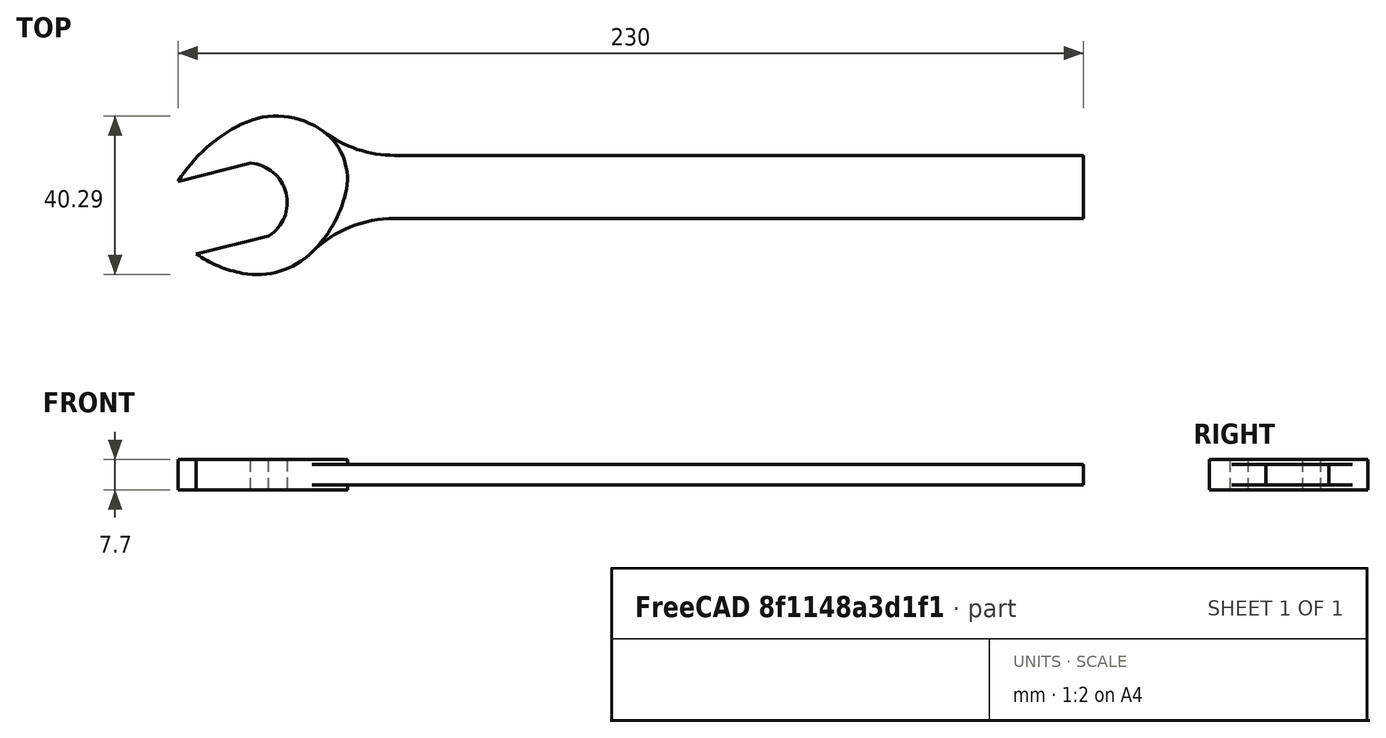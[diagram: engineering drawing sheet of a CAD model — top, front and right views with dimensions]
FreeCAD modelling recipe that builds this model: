
FCSTD DOCUMENT  (FreeCAD 0.21R33694 (Git))
Label: Spanner_Example
License: All rights reserved
LicenseURL: http://en.wikipedia.org/wiki/All_rights_reserved
objects: Sketcher::SketchObject×2, PartDesign::Pad×2, Fem::ConstraintFixed×2, PartDesign::Body×1, Fem::FemSolverObjectPython×1, Fem::FemMeshObjectPython×1, App::MaterialObjectPython×1, Fem::ConstraintPressure×1, Fem::FemAnalysis×1
note: 7 computed .brp shape members not serialized (recipe doc carries the construction recipe); baked Part::Feature solids carry a one-line shape summary decoded from their .brp

FEATURE [Sketcher::SketchObject] Sketch
  FullyConstrained = false
  MapMode = 5
  Support = -> [XY_Plane]
  sketch-geometry (10):
    g0: LineSegment StartX=-55 StartY=18.4356 StartZ=0 EndX=-36.5644 EndY=23.0321 EndZ=0
    g1: LineSegment StartX=-50.4035 StartY=-3.6e-15 StartZ=0 EndX=-31.9679 EndY=4.59652 EndZ=0
    g2: LineSegment StartX=-31.9679 StartY=4.59652 StartZ=0 EndX=-36.5644 EndY=23.0321 EndZ=0
    g3: ArcOfCircle CenterX=-37.2959 CenterY=13.0589 CenterZ=0 NormalX=0 NormalY=0 NormalZ=1 AngleXU=0 Radius=10 StartAngle=5.2743 EndAngle=7.78077
    g4: ArcOfCircle CenterX=-21.1751 CenterY=-2.91558 CenterZ=0 NormalX=0 NormalY=0 NormalZ=1 AngleXU=0 Radius=40 StartAngle=2.02778 EndAngle=2.57853
    g5: ArcOfCircle CenterX=-30 CenterY=15.0321 CenterZ=0 NormalX=0 NormalY=0 NormalZ=1 AngleXU=0 Radius=20 StartAngle=0.927295 EndAngle=2.02778
    g6: ArcOfCircle CenterX=-33.1975 CenterY=24.5755 CenterZ=0 NormalX=0 NormalY=0 NormalZ=1 AngleXU=0 Radius=30 StartAngle=4.10158 EndAngle=4.53115
    g7: ArcOfCircle CenterX=-35 CenterY=14.7393 CenterZ=0 NormalX=0 NormalY=0 NormalZ=1 AngleXU=0 Radius=20 StartAngle=4.53115 EndAngle=5.48779
    g8: ArcOfCircle CenterX=-27 CenterY=19.0321 CenterZ=0 NormalX=0 NormalY=0 NormalZ=1 AngleXU=0 Radius=15 StartAngle=6.03904 EndAngle=7.21048
    g9: ArcOfCircle CenterX=-43.1518 CenterY=23.0558 CenterZ=0 NormalX=0 NormalY=0 NormalZ=1 AngleXU=0 Radius=31.6454 StartAngle=5.48779 EndAngle=6.03904
  constraints (26):
    c: Parallel(g0,g1)
    c: Distance(g0) = 19
    c: Distance(g1) = 19
    c: Distance(g1,g0) = 19
    c: Coincident(g2,g1)
    c: Coincident(g2,g0)
    c: Perpendicular(g0,g2)
    c: Angle(g-1,g0) = 0.244346
    c: PointOnObject(g1,g-1)
    c: Coincident(g3,g0)
    c: Coincident(g3,g1)
    c: Radius(g3) = 10
    c: Coincident(g4,g0)
    c: Radius(g4) = 40
    c: Radius(g5) = 20
    c: Coincident(g6,g1)
    c: Radius(g6) = 30
    c: Radius(g7) = 20
    c: Tangent(g5,g4) = -1.5708
    c: Tangent(g7,g6) = -1.5708
    c: Distance(g7,g-2) = 21
    c: Distance(g5,g-2) = 18
    c: Tangent(g8,g5) = -1.5708
    c: Radius(g8) = 15
    c: Tangent(g9,g7) = -1.5708
    c: Tangent(g9,g8) = -1.5708
FEATURE [Sketcher::SketchObject] Sketch001
  FullyConstrained = false
  MapMode = 5
  Support = -> [XY_Plane]
  sketch-geometry (9):
    g0: ArcOfCircle CenterX=1e-16 CenterY=55.0321 CenterZ=0 NormalX=0 NormalY=0 NormalZ=1 AngleXU=0 Radius=30 StartAngle=4.06889 EndAngle=4.71239
    g1: LineSegment StartX=-5.4e-15 StartY=25.0321 StartZ=0 EndX=140 EndY=25.0321 EndZ=0
    g2: ArcOfCircle CenterX=-3.7e-15 CenterY=-20.9679 CenterZ=0 NormalX=0 NormalY=0 NormalZ=1 AngleXU=0 Radius=30 StartAngle=1.5708 EndAngle=2.34619
    g3: LineSegment StartX=-1.9e-15 StartY=9.03213 StartZ=0 EndX=140 EndY=9.03213 EndZ=0
    g4: LineSegment StartX=140 StartY=25.0321 StartZ=0 EndX=175 EndY=25.0321 EndZ=0
    g5: LineSegment StartX=140 StartY=9.03213 StartZ=0 EndX=175 EndY=9.03213 EndZ=0
    g6: LineSegment StartX=175 StartY=25.0321 StartZ=0 EndX=175 EndY=9.03213 EndZ=0
    g7: ArcOfCircle CenterX=-27 CenterY=19.0321 CenterZ=0 NormalX=0 NormalY=0 NormalZ=1 AngleXU=0 Radius=15 StartAngle=6.03904 EndAngle=7.21048
    g8: ArcOfCircle CenterX=-43.1518 CenterY=23.0558 CenterZ=0 NormalX=0 NormalY=0 NormalZ=1 AngleXU=0 Radius=31.6454 StartAngle=5.48779 EndAngle=6.03904
  constraints (20):
    c: Radius(g0) = 30
    c: Horizontal(g1)
    c: Radius(g2) = 30
    c: Horizontal(g3)
    c: Distance(g2,g1) = 16
    c: Tangent(g1,g0) = -1.5708
    c: Tangent(g3,g2) = 1.5708
    c: PointOnObject(g2,g-2)
    c: Distance(g1) = 140
    c: Distance(g3) = 140
    c: Coincident(g4,g1)
    c: Horizontal(g4)
    c: Coincident(g5,g3)
    c: Horizontal(g5)
    c: Coincident(g6,g4)
    c: Coincident(g6,g5)
    c: Vertical(g6)
    c: Distance(g4) = 35
    c: Radius(g7) = 15
    c: Tangent(g8,g7) = -1.5708
FEATURE [PartDesign::Pad] Pad
  Direction = (0,0,1)
  Length = 5.3
  Length2 = 10
  Midplane = true
  Profile = -> Sketch001
  ReferenceAxis = -> Sketch001 [N_Axis]
  Type = 0
FEATURE [PartDesign::Pad] Pad001
  BaseFeature = -> Pad
  Direction = (0,0,1)
  Length = 7.7
  Length2 = 10
  Midplane = true
  Profile = -> Sketch
  ReferenceAxis = -> Sketch [N_Axis]
  Type = 0
FEATURE [PartDesign::Body] Body
  Group = -> [Sketch,Sketch001,Pad,Pad001]
  Origin = -> Origin
  Tip = -> Pad001
FEATURE [Fem::FemSolverObjectPython] SolverCcxTools  # FEM object (typed FeaturePython)
  AnalysisType = 0
  BeamShellResultOutput3D = false
  BucklingFactors = 1
  EigenmodeHighLimit = 1000000
  EigenmodeLowLimit = 0
  EigenmodesCount = 10
  GeometricalNonlinearity = 1
  IterationsControlParameterCutb = 0.25,0.5,0.75,0.85,,,1.5,
  IterationsControlParameterIter = 4,8,9,200,10,400,,200,,
  IterationsControlParameterTimeUse = false
  IterationsThermoMechMaximum = 2000
  IterationsUserDefinedIncrementations = false
  IterationsUserDefinedTimeStepLength = false
  MaterialNonlinearity = 1
  MatrixSolverType = 0
  SplitInputWriter = false
  ThermoMechSteadyState = true
  TimeEnd = 1
  TimeInitialStep = 0.01
FEATURE [Fem::FemMeshObjectPython] FEMMeshGmsh  # FEM object (typed FeaturePython)
  Algorithm2D = 0
  Algorithm3D = 0
  CharacteristicLengthMax = 5
  CharacteristicLengthMin = 0
  CoherenceMesh = true
  ElementDimension = 0
  ElementOrder = 1
  GeometryTolerance = 1e-06
  GroupsOfNodes = false
  HighOrderOptimize = 0
  MeshSizeFromCurvature = 12
  OptimizeNetgen = false
  OptimizeStd = true
  Part = -> Body
  RecombinationAlgorithm = 0
  Recombine3DAll = false
  RecombineAll = false
  SecondOrderLinear = false
FEATURE [App::MaterialObjectPython] MaterialSolid  # material (typed FeaturePython)
  Category = 0
  Material = AuthorAndLicense=(c) 2013 Juergen Riegel (CC-BY 3.0),CardName=Steel-Generic,Density=7900 kg/m^3,+9 more (map truncated)
  References = -> [Pad001]
FEATURE [Fem::ConstraintPressure] ConstraintPressure
  NormalDirection = (0,1,0)
  Normals = (12) [(0,1,0),(0,1,0),(0,1,0),(0,1,0),(0,1,0),(0,1,0),(0,1,0),(0,1,0),(0,1,0),(0,1,0),(0,1,0),(0,1,0)]
  Points = (12) [(140,25.0321,2.65),(151.667,25.0321,2.65),(163.333,25.0321,2.65),(175,25.0321,2.65),(140,25.0321,0),(151.667,25.0321,0),(163.333,25.0321,0),+5 more]
  Pressure = 20
  References = -> [Pad001]
  Scale = 3
FEATURE [Fem::ConstraintFixed] ConstraintFixed
  NormalDirection = (-0.241922,0.970296,0)
  Normals = (9) [(-0.241922,0.970296,0),(-0.241922,0.970296,0),(-0.241922,0.970296,0),(-0.241922,0.970296,0),(-0.241922,0.970296,0),(-0.241922,0.970296,0),+3 more]
  Points = (9) [(-50.4035,-3.55e-15,3.85),(-41.1857,2.29826,3.85),(-31.9679,4.59652,3.85),(-50.4035,-3.55e-15,0),(-41.1857,2.29826,0),(-31.9679,4.59652,0),+3 more]
  References = -> [Pad001]
FEATURE [Fem::ConstraintFixed] ConstraintFixed001
  NormalDirection = (0,0,1)
  Normals = (2) [(0,0,1),(0,0,1)]
  Points = (2) [(-36.5644,23.0321,-3.85),(-36.5644,23.0321,3.85)]
  References = -> [Pad001]
FEATURE [Fem::FemAnalysis] Analysis
  Group = -> [SolverCcxTools,FEMMeshGmsh,MaterialSolid,ConstraintPressure,ConstraintFixed,ConstraintFixed001]
